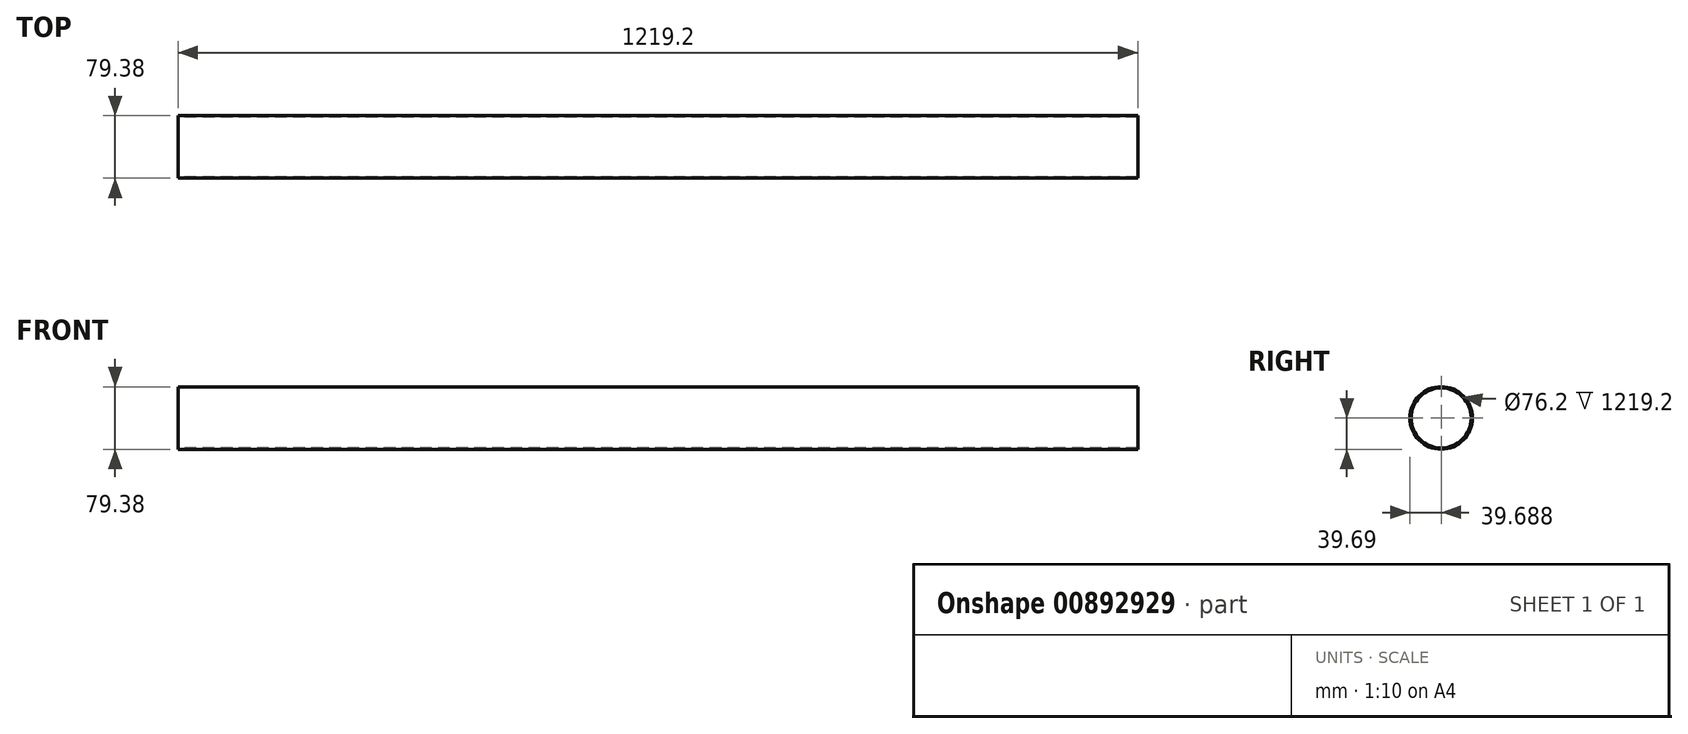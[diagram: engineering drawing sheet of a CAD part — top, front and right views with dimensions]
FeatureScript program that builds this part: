
annotation { "Feature Type Name" : "Feature", "Feature Type Description" : "" }
export const myFeature = defineFeature(function(context is Context, id is Id, definition is map)
    precondition{}
    {
        {
            var Q0;
            Q0=qCreatedBy(makeId("Top.planeOp"),FACE);
            var sketch = newSketch(context, id + "F0", { "sketchPlane" : qUnion([Q0])});
            skLineSegment(sketch, "E0", {"start": v(0, 0) * mm, "end": v(-558.8, 0) * mm, "construction": true});
            skLineSegment(sketch, "E1", {"start": v(0, 0) * mm, "end": v(558.8, 0) * mm});
            skLineSegment(sketch, "E2", {"start": v(0, 0) * mm, "end": v(0, -965.2) * mm, "construction": true});
            skLineSegment(sketch, "E3", {"start": v(0, -965.2) * mm, "end": v(-88.9, -965.2) * mm, "construction": true});
            skLineSegment(sketch, "E4", {"start": v(0, -965.2) * mm, "end": v(88.9, -965.2) * mm, "construction": true});
            skLineSegment(sketch, "E5", {"start": v(-558.8, 0) * mm, "end": v(-88.9, -965.2) * mm, "construction": true});
            skLineSegment(sketch, "E6", {"start": v(558.8, 0) * mm, "end": v(88.9, -965.2) * mm, "construction": true});
            skLineSegment(sketch, "E7", {"start": v(-558.8, 0) * mm, "end": v(-558.8, 39.69) * mm});
            skLineSegment(sketch, "E8", {"start": v(-558.8, 0) * mm, "end": v(-533.93, -51.1) * mm});
            skCircle(sketch, "E9", {"center": v(-517.66, -26.62) * mm, "radius": 22.23 * mm});
            skLineSegment(sketch, "E10", {"start": v(-533.93, -51.1) * mm, "end": v(0, 0) * mm});
            skLineSegment(sketch, "E11.0", {"start": v(0, 39.67) * mm, "end": v(-558.8, 39.67) * mm});
            skSolve(sketch);
        }
        {
            var Q0;
            Q0=sQuery(id+"F0.wireOp",VERTEX,"E7.end");
            var Q1;
            Q1=qCreatedBy(makeId("Right.planeOp"),FACE);
            cPlane(context, id + "F1", {"entities" : qUnion([Q0, Q1]), "cplaneType" : CPlaneType.PLANE_POINT, "offset" : 25.4 * mm, "width" : 152.4 * mm, "height" : 152.4 * mm});
        }
        {
            var Q0;
            Q0=qCreatedBy(id+"F1.planeOp",FACE);
            var sketch = newSketch(context, id + "F2", { "sketchPlane" : qUnion([Q0])});
            skCircle(sketch, "E12", {"center": v(39.69, 0) * mm, "radius": 39.69 * mm});
            skCircle(sketch, "E13", {"center": v(39.69, 0) * mm, "radius": 38.1 * mm});
            skSolve(sketch);
        }
        {
            var Q0;
            Q0=makeQuery(id+"F2.imprint","IMPRINT",FACE,{"disambiguationData":[TD([[makeQuery(id+"F2.imprint","IMPRINT",EDGE,{"derivedFrom":sQuery(id+"F2.wireOp",EDGE,"E12")}),1.0]])]});
            extrude(context, id + "F3", {"entities" : qUnion([Q0]), "depth" : 1219.2 * mm, "offsetDistance" : 25.4 * mm});
        }
    });
